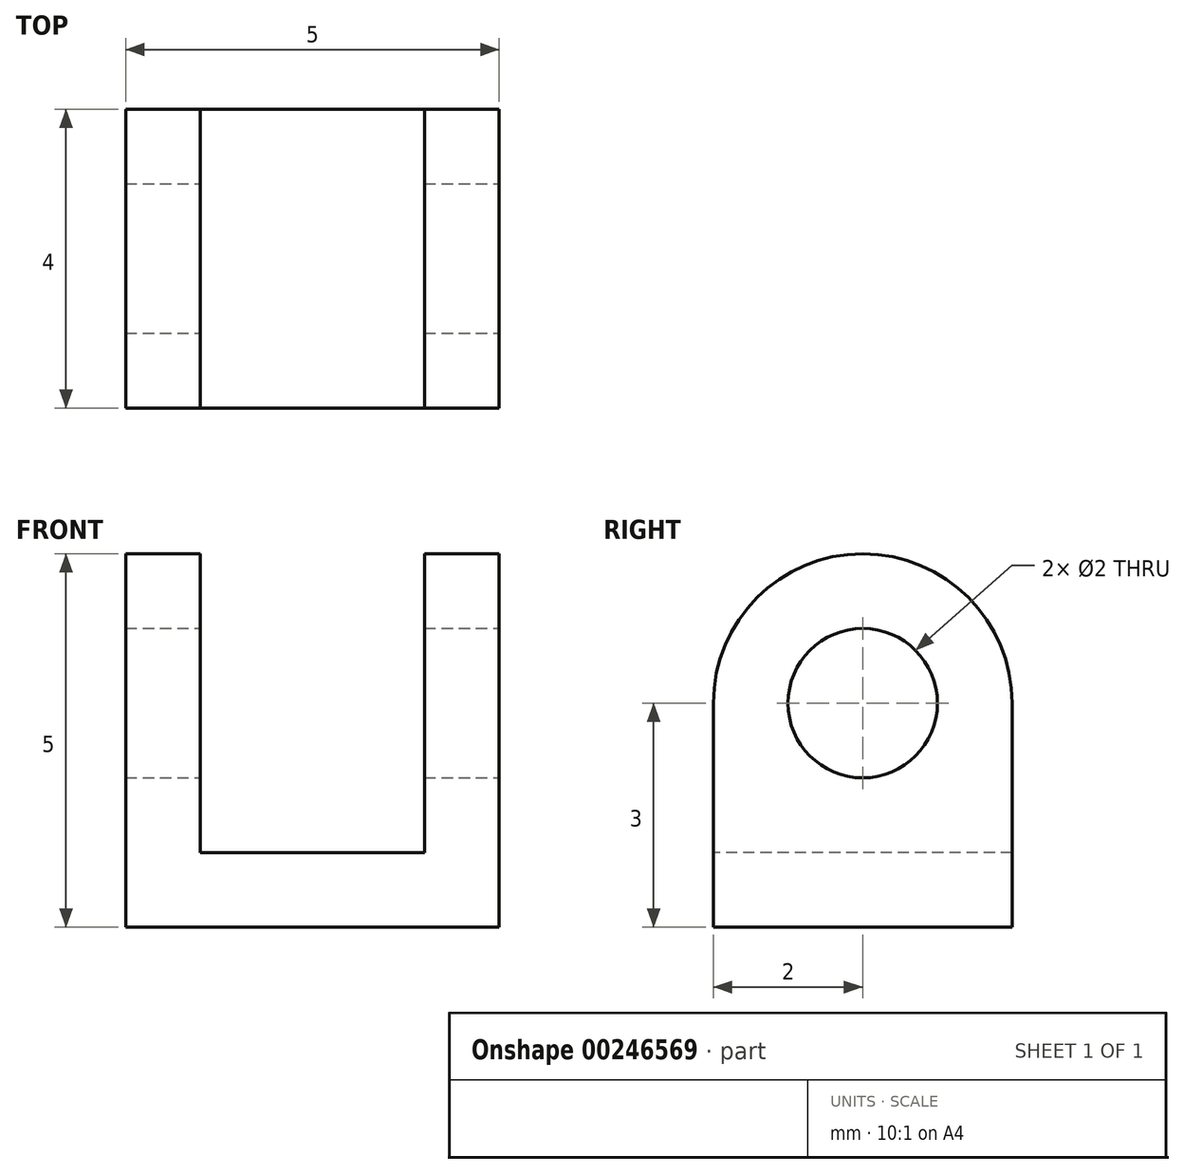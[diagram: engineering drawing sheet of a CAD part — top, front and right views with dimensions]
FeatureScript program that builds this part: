
annotation { "Feature Type Name" : "Feature", "Feature Type Description" : "" }
export const myFeature = defineFeature(function(context is Context, id is Id, definition is map)
    precondition{}
    {
        {
            var Q0;
            Q0=qCreatedBy(makeId("Top.planeOp"),FACE);
            var sketch = newSketch(context, id + "F0", { "sketchPlane" : qUnion([Q0])});
            skLineSegment(sketch, "E0.bottom", {"start": v(0, 0) * mm, "end": v(5, 0) * mm});
            skLineSegment(sketch, "E0.top", {"start": v(0, 4) * mm, "end": v(5, 4) * mm});
            skLineSegment(sketch, "E0.left", {"start": v(0, 0) * mm, "end": v(0, 4) * mm});
            skLineSegment(sketch, "E0.right", {"start": v(5, 0) * mm, "end": v(5, 4) * mm});
            skSolve(sketch);
        }
        {
            var Q0;
            Q0=makeQuery(id+"F0.imprint","IMPRINT",FACE,{"disambiguationData":[TD([[makeQuery(id+"F0.imprint","IMPRINT",EDGE,{"derivedFrom":sQuery(id+"F0.wireOp",EDGE,"E0.bottom")}),1.0]])]});
            extrude(context, id + "F1", {"entities" : qUnion([Q0]), "depth" : 1 * mm});
        }
        {
            var Q0;
            Q0=makeQuery(id+"F1.opExtrude","CAP_FACE",FACE,{"disambiguationData":[OSD([sQuery(id+"F0.wireOp",EDGE,"E0.bottom"),sQuery(id+"F0.wireOp",EDGE,"E0.top"),sQuery(id+"F0.wireOp",EDGE,"E0.left"),sQuery(id+"F0.wireOp",EDGE,"E0.right")])],"isStart":false});
            var sketch = newSketch(context, id + "F2", { "sketchPlane" : qUnion([Q0])});
            skLineSegment(sketch, "E1.bottom", {"start": v(0, 4) * mm, "end": v(1, 4) * mm});
            skLineSegment(sketch, "E1.top", {"start": v(0, 0) * mm, "end": v(1, 0) * mm});
            skLineSegment(sketch, "E1.left", {"start": v(0, 4) * mm, "end": v(0, 0) * mm});
            skLineSegment(sketch, "E1.right", {"start": v(1, 4) * mm, "end": v(1, 0) * mm});
            skLineSegment(sketch, "E2.bottom", {"start": v(5, 4) * mm, "end": v(4, 4) * mm});
            skLineSegment(sketch, "E2.top", {"start": v(5, 0) * mm, "end": v(4, 0) * mm});
            skLineSegment(sketch, "E2.left", {"start": v(5, 4) * mm, "end": v(5, 0) * mm});
            skLineSegment(sketch, "E2.right", {"start": v(4, 4) * mm, "end": v(4, 0) * mm});
            skSolve(sketch);
        }
        {
            var Q0;
            Q0=makeQuery(id+"F2.imprint","IMPRINT",FACE,{"disambiguationData":[TD([[makeQuery(id+"F2.imprint","IMPRINT",EDGE,{"derivedFrom":sQuery(id+"F2.wireOp",EDGE,"E1.bottom")}),-1.0]])]});
            var Q1;
            Q1=makeQuery(id+"F2.imprint","IMPRINT",FACE,{"disambiguationData":[TD([[makeQuery(id+"F2.imprint","IMPRINT",EDGE,{"derivedFrom":sQuery(id+"F2.wireOp",EDGE,"E2.bottom")}),-1.0]])]});
            extrude(context, id + "F3", {"entities" : qUnion([Q0, Q1]), "operationType" : NewBodyOperationType.ADD, "depth" : 5 * mm});
        }
        {
            var Q0;
            Q0=makeQuery(id+"F3.boolean.opBoolean","MERGE",FACE,{"derivedFrom":[makeQuery(id+"F1.opExtrude","SWEPT_FACE",FACE,{"disambiguationData":[OSD([sQuery(id+"F0.wireOp",EDGE,"E0.right")])]}),makeQuery(id+"F3.opExtrude","SWEPT_FACE",FACE,{"disambiguationData":[OSD([sQuery(id+"F2.wireOp",EDGE,"E2.left")])]})]});
            var sketch = newSketch(context, id + "F4", { "sketchPlane" : qUnion([Q0])});
            skLineSegment(sketch, "E3.bottom", {"start": v(0, 0) * mm, "end": v(4, 0) * mm});
            skLineSegment(sketch, "E3.left", {"start": v(0, 0) * mm, "end": v(0, 3) * mm});
            skArc(sketch, "E4", {"start": v(4, 3) * mm, "mid": v(2, 5) * mm, "end": v(0, 3) * mm});
            skCircle(sketch, "E5", {"center": v(2, 3) * mm, "radius": 1 * mm});
            skLineSegment(sketch, "E6", {"start": v(4, 0) * mm, "end": v(4, 3) * mm});
            skSolve(sketch);
        }
        {
            var Q0;
            {var subQ2=sQuery(id+"F2.wireOp",EDGE,"E2.left");var subQ8=makeQuery(id+"F3.opExtrude","CAP_EDGE",EDGE,{"disambiguationData":[OSD([subQ2])],"isStart":false});Q0=makeQuery(id+"F4.imprint","IMPRINT",FACE,{"disambiguationData":[TD([[makeQuery(id+"F4.imprint","IMPRINT",EDGE,{"derivedFrom":subQ8}),-1.0]])]});}
            extrude(context, id + "F5", {"entities" : qUnion([Q0]), "operationType" : NewBodyOperationType.REMOVE, "oppositeDirection" : true, "depth" : 25 * mm});
        }
        {
            var Q0;
            Q0=makeQuery(id+"F4.imprint","IMPRINT",FACE,{"disambiguationData":[TD([[makeQuery(id+"F4.imprint","IMPRINT",EDGE,{"derivedFrom":sQuery(id+"F4.wireOp",EDGE,"E5")}),1.0]])]});
            var Q1;
            Q1=sQuery(id+"F4.wireOp",EDGE,"E5");
            extrude(context, id + "F6", {"entities" : qUnion([Q0]), "operationType" : NewBodyOperationType.REMOVE, "surfaceEntities" : qUnion([Q1]), "oppositeDirection" : true, "depth" : 25 * mm});
        }
    });
